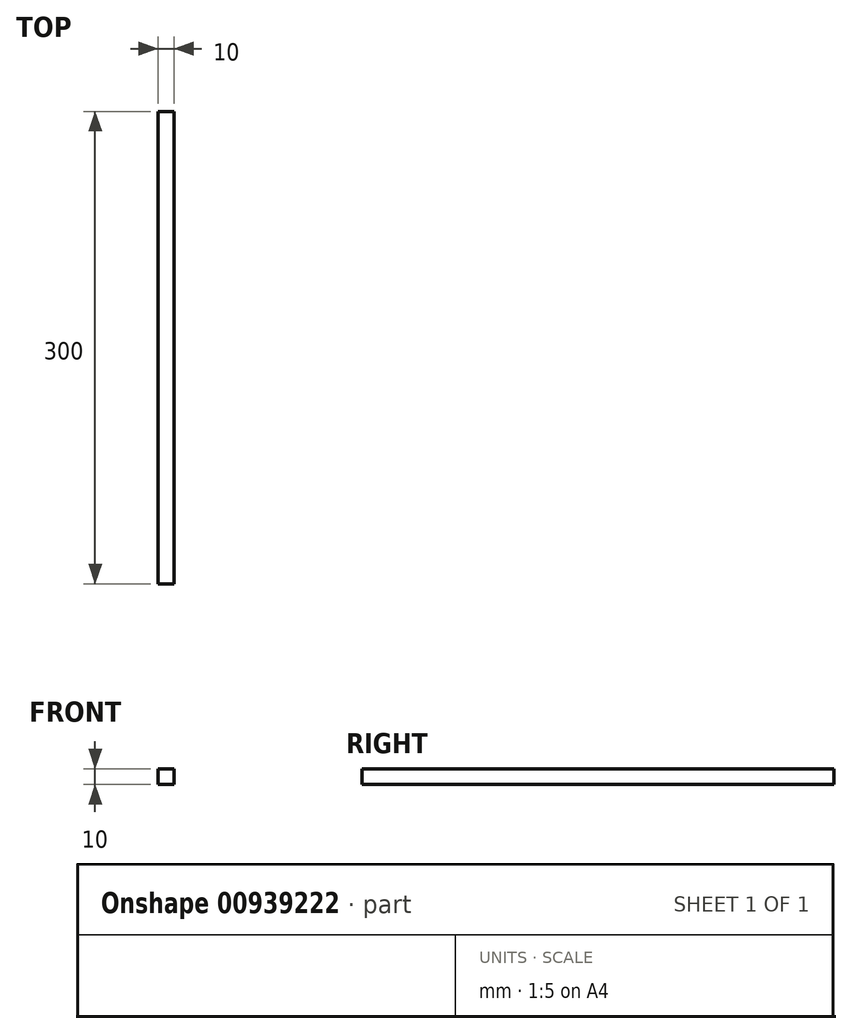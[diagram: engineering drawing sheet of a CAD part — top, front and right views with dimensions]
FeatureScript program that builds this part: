
annotation { "Feature Type Name" : "Feature", "Feature Type Description" : "" }
export const myFeature = defineFeature(function(context is Context, id is Id, definition is map)
    precondition{}
    {
        {
            var Q0;
            Q0=qCreatedBy(makeId("Front.planeOp"),FACE);
            var sketch = newSketch(context, id + "F0", { "sketchPlane" : qUnion([Q0])});
            skLineSegment(sketch, "E0.bottom", {"start": v(5, 5) * mm, "end": v(-5, 5) * mm});
            skLineSegment(sketch, "E0.top", {"start": v(5, -5) * mm, "end": v(-5, -5) * mm});
            skLineSegment(sketch, "E0.left", {"start": v(5, 5) * mm, "end": v(5, -5) * mm});
            skLineSegment(sketch, "E0.right", {"start": v(-5, 5) * mm, "end": v(-5, -5) * mm});
            skPoint(sketch, "E0.middle", {"position": v(0, 0) * mm});
            skSolve(sketch);
        }
        {
            var Q0;
            Q0=makeQuery(id+"F0.imprint","IMPRINT",FACE,{"disambiguationData":[TD([[makeQuery(id+"F0.imprint","IMPRINT",EDGE,{"derivedFrom":sQuery(id+"F0.wireOp",EDGE,"E0.bottom")}),1.0]])]});
            extrude(context, id + "F1", {"entities" : qUnion([Q0]), "depth" : 300 * mm, "offsetDistance" : 25 * mm});
        }
    });
